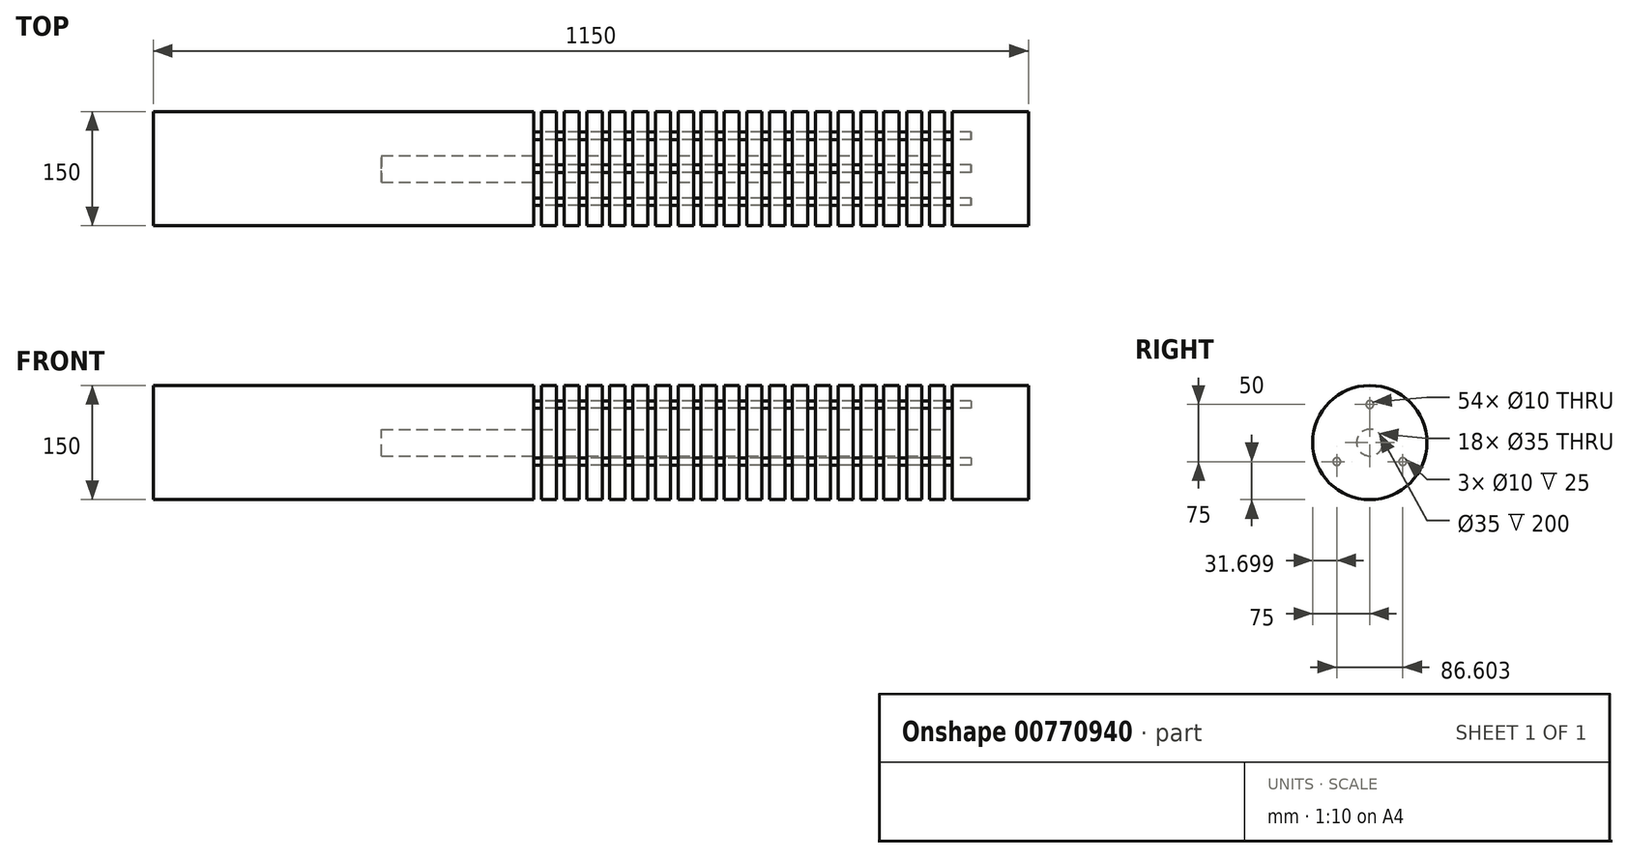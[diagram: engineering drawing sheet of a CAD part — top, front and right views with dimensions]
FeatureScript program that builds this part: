
annotation { "Feature Type Name" : "Feature", "Feature Type Description" : "" }
export const myFeature = defineFeature(function(context is Context, id is Id, definition is map)
    precondition{}
    {
        {
            var Q0;
            Q0=qCreatedBy(makeId("Top.planeOp"),FACE);
            var sketch = newSketch(context, id + "F0", { "sketchPlane" : qUnion([Q0])});
            skLineSegment(sketch, "E0", {"start": v(-500, 0) * mm, "end": v(-500, -75) * mm});
            skLineSegment(sketch, "E1", {"start": v(-500, -75) * mm, "end": v(0, -75) * mm});
            skLineSegment(sketch, "E2", {"start": v(0, -75) * mm, "end": v(0, -17.5) * mm});
            skLineSegment(sketch, "E3", {"start": v(0, -17.5) * mm, "end": v(-200, -17.5) * mm});
            skLineSegment(sketch, "E4", {"start": v(-200, -17.5) * mm, "end": v(-200, 0) * mm});
            skLineSegment(sketch, "E5", {"start": v(-200, 0) * mm, "end": v(-500, 0) * mm});
            skSolve(sketch);
        }
        {
            var Q0;
            Q0=qCreatedBy(makeId("Top.planeOp"),FACE);
            var sketch = newSketch(context, id + "F1", { "sketchPlane" : qUnion([Q0])});
            skLineSegment(sketch, "E6.bottom", {"start": v(10, -17.5) * mm, "end": v(30, -17.5) * mm});
            skLineSegment(sketch, "E6.top", {"start": v(10, -75) * mm, "end": v(30, -75) * mm});
            skLineSegment(sketch, "E6.left", {"start": v(10, -17.5) * mm, "end": v(10, -75) * mm});
            skLineSegment(sketch, "E6.right", {"start": v(30, -17.5) * mm, "end": v(30, -75) * mm});
            skLineSegment(sketch, "E7.1.0.0", {"start": v(40, -75) * mm, "end": v(60, -75) * mm});
            skLineSegment(sketch, "E7.1.0.1", {"start": v(60, -17.5) * mm, "end": v(60, -75) * mm});
            skLineSegment(sketch, "E7.1.0.2", {"start": v(40, -17.5) * mm, "end": v(40, -75) * mm});
            skLineSegment(sketch, "E7.1.0.3", {"start": v(40, -17.5) * mm, "end": v(60, -17.5) * mm});
            skLineSegment(sketch, "E7.2.0.0", {"start": v(70, -75) * mm, "end": v(90, -75) * mm});
            skLineSegment(sketch, "E7.2.0.1", {"start": v(90, -17.5) * mm, "end": v(90, -75) * mm});
            skLineSegment(sketch, "E7.2.0.2", {"start": v(70, -17.5) * mm, "end": v(70, -75) * mm});
            skLineSegment(sketch, "E7.2.0.3", {"start": v(70, -17.5) * mm, "end": v(90, -17.5) * mm});
            skLineSegment(sketch, "E7.3.0.0", {"start": v(100, -75) * mm, "end": v(120, -75) * mm});
            skLineSegment(sketch, "E7.3.0.1", {"start": v(120, -17.5) * mm, "end": v(120, -75) * mm});
            skLineSegment(sketch, "E7.3.0.2", {"start": v(100, -17.5) * mm, "end": v(100, -75) * mm});
            skLineSegment(sketch, "E7.3.0.3", {"start": v(100, -17.5) * mm, "end": v(120, -17.5) * mm});
            skLineSegment(sketch, "E7.4.0.0", {"start": v(130, -75) * mm, "end": v(150, -75) * mm});
            skLineSegment(sketch, "E7.4.0.1", {"start": v(150, -17.5) * mm, "end": v(150, -75) * mm});
            skLineSegment(sketch, "E7.4.0.2", {"start": v(130, -17.5) * mm, "end": v(130, -75) * mm});
            skLineSegment(sketch, "E7.4.0.3", {"start": v(130, -17.5) * mm, "end": v(150, -17.5) * mm});
            skLineSegment(sketch, "E7.5.0.0", {"start": v(160, -75) * mm, "end": v(180, -75) * mm});
            skLineSegment(sketch, "E7.5.0.1", {"start": v(180, -17.5) * mm, "end": v(180, -75) * mm});
            skLineSegment(sketch, "E7.5.0.2", {"start": v(160, -17.5) * mm, "end": v(160, -75) * mm});
            skLineSegment(sketch, "E7.5.0.3", {"start": v(160, -17.5) * mm, "end": v(180, -17.5) * mm});
            skLineSegment(sketch, "E7.6.0.0", {"start": v(190, -75) * mm, "end": v(210, -75) * mm});
            skLineSegment(sketch, "E7.6.0.1", {"start": v(210, -17.5) * mm, "end": v(210, -75) * mm});
            skLineSegment(sketch, "E7.6.0.2", {"start": v(190, -17.5) * mm, "end": v(190, -75) * mm});
            skLineSegment(sketch, "E7.6.0.3", {"start": v(190, -17.5) * mm, "end": v(210, -17.5) * mm});
            skLineSegment(sketch, "E7.7.0.0", {"start": v(220, -75) * mm, "end": v(240, -75) * mm});
            skLineSegment(sketch, "E7.7.0.1", {"start": v(240, -17.5) * mm, "end": v(240, -75) * mm});
            skLineSegment(sketch, "E7.7.0.2", {"start": v(220, -17.5) * mm, "end": v(220, -75) * mm});
            skLineSegment(sketch, "E7.7.0.3", {"start": v(220, -17.5) * mm, "end": v(240, -17.5) * mm});
            skLineSegment(sketch, "E7.8.0.0", {"start": v(250, -75) * mm, "end": v(270, -75) * mm});
            skLineSegment(sketch, "E7.8.0.1", {"start": v(270, -17.5) * mm, "end": v(270, -75) * mm});
            skLineSegment(sketch, "E7.8.0.2", {"start": v(250, -17.5) * mm, "end": v(250, -75) * mm});
            skLineSegment(sketch, "E7.8.0.3", {"start": v(250, -17.5) * mm, "end": v(270, -17.5) * mm});
            skLineSegment(sketch, "E7.9.0.0", {"start": v(280, -75) * mm, "end": v(300, -75) * mm});
            skLineSegment(sketch, "E7.9.0.1", {"start": v(300, -17.5) * mm, "end": v(300, -75) * mm});
            skLineSegment(sketch, "E7.9.0.2", {"start": v(280, -17.5) * mm, "end": v(280, -75) * mm});
            skLineSegment(sketch, "E7.9.0.3", {"start": v(280, -17.5) * mm, "end": v(300, -17.5) * mm});
            skLineSegment(sketch, "E7.10.0.0", {"start": v(310, -75) * mm, "end": v(330, -75) * mm});
            skLineSegment(sketch, "E7.10.0.1", {"start": v(330, -17.5) * mm, "end": v(330, -75) * mm});
            skLineSegment(sketch, "E7.10.0.2", {"start": v(310, -17.5) * mm, "end": v(310, -75) * mm});
            skLineSegment(sketch, "E7.10.0.3", {"start": v(310, -17.5) * mm, "end": v(330, -17.5) * mm});
            skLineSegment(sketch, "E7.11.0.0", {"start": v(340, -75) * mm, "end": v(360, -75) * mm});
            skLineSegment(sketch, "E7.11.0.1", {"start": v(360, -17.5) * mm, "end": v(360, -75) * mm});
            skLineSegment(sketch, "E7.11.0.2", {"start": v(340, -17.5) * mm, "end": v(340, -75) * mm});
            skLineSegment(sketch, "E7.11.0.3", {"start": v(340, -17.5) * mm, "end": v(360, -17.5) * mm});
            skLineSegment(sketch, "E7.12.0.0", {"start": v(370, -75) * mm, "end": v(390, -75) * mm});
            skLineSegment(sketch, "E7.12.0.1", {"start": v(390, -17.5) * mm, "end": v(390, -75) * mm});
            skLineSegment(sketch, "E7.12.0.2", {"start": v(370, -17.5) * mm, "end": v(370, -75) * mm});
            skLineSegment(sketch, "E7.12.0.3", {"start": v(370, -17.5) * mm, "end": v(390, -17.5) * mm});
            skLineSegment(sketch, "E7.13.0.0", {"start": v(400, -75) * mm, "end": v(420, -75) * mm});
            skLineSegment(sketch, "E7.13.0.1", {"start": v(420, -17.5) * mm, "end": v(420, -75) * mm});
            skLineSegment(sketch, "E7.13.0.2", {"start": v(400, -17.5) * mm, "end": v(400, -75) * mm});
            skLineSegment(sketch, "E7.13.0.3", {"start": v(400, -17.5) * mm, "end": v(420, -17.5) * mm});
            skLineSegment(sketch, "E7.14.0.0", {"start": v(430, -75) * mm, "end": v(450, -75) * mm});
            skLineSegment(sketch, "E7.14.0.1", {"start": v(450, -17.5) * mm, "end": v(450, -75) * mm});
            skLineSegment(sketch, "E7.14.0.2", {"start": v(430, -17.5) * mm, "end": v(430, -75) * mm});
            skLineSegment(sketch, "E7.14.0.3", {"start": v(430, -17.5) * mm, "end": v(450, -17.5) * mm});
            skLineSegment(sketch, "E7.15.0.0", {"start": v(460, -75) * mm, "end": v(480, -75) * mm});
            skLineSegment(sketch, "E7.15.0.1", {"start": v(480, -17.5) * mm, "end": v(480, -75) * mm});
            skLineSegment(sketch, "E7.15.0.2", {"start": v(460, -17.5) * mm, "end": v(460, -75) * mm});
            skLineSegment(sketch, "E7.15.0.3", {"start": v(460, -17.5) * mm, "end": v(480, -17.5) * mm});
            skLineSegment(sketch, "E7.16.0.0", {"start": v(490, -75) * mm, "end": v(510, -75) * mm});
            skLineSegment(sketch, "E7.16.0.1", {"start": v(510, -17.5) * mm, "end": v(510, -75) * mm});
            skLineSegment(sketch, "E7.16.0.2", {"start": v(490, -17.5) * mm, "end": v(490, -75) * mm});
            skLineSegment(sketch, "E7.16.0.3", {"start": v(490, -17.5) * mm, "end": v(510, -17.5) * mm});
            skLineSegment(sketch, "E7.17.0.0", {"start": v(520, -75) * mm, "end": v(540, -75) * mm});
            skLineSegment(sketch, "E7.17.0.1", {"start": v(540, -17.5) * mm, "end": v(540, -75) * mm});
            skLineSegment(sketch, "E7.17.0.2", {"start": v(520, -17.5) * mm, "end": v(520, -75) * mm});
            skLineSegment(sketch, "E7.17.0.3", {"start": v(520, -17.5) * mm, "end": v(540, -17.5) * mm});
            skLineSegment(sketch, "E7.direction1", {"start": v(10, -75) * mm, "end": v(40, -75) * mm, "construction": true});
            skSolve(sketch);
        }
        {
            var Q0;
            Q0=qCreatedBy(makeId("Top.planeOp"),FACE);
            var sketch = newSketch(context, id + "F2", { "sketchPlane" : qUnion([Q0])});
            skLineSegment(sketch, "E8.bottom", {"start": v(550, -75) * mm, "end": v(650, -75) * mm});
            skLineSegment(sketch, "E8.top", {"start": v(550, 0) * mm, "end": v(650, 0) * mm});
            skLineSegment(sketch, "E8.left", {"start": v(550, -75) * mm, "end": v(550, 0) * mm});
            skLineSegment(sketch, "E8.right", {"start": v(650, -75) * mm, "end": v(650, 0) * mm});
            skSolve(sketch);
        }
        {
            var Q0;
            Q0=makeQuery(id+"F0.imprint","IMPRINT",FACE,{"disambiguationData":[TD([[makeQuery(id+"F0.imprint","IMPRINT",EDGE,{"derivedFrom":sQuery(id+"F0.wireOp",EDGE,"E0")}),1.0]])]});
            var Q1;
            Q1=makeQuery(id+"F1.imprint","IMPRINT",FACE,{"disambiguationData":[TD([[makeQuery(id+"F1.imprint","IMPRINT",EDGE,{"derivedFrom":sQuery(id+"F1.wireOp",EDGE,"E7.4.0.0")}),1.0]])]});
            var Q2;
            Q2=makeQuery(id+"F1.imprint","IMPRINT",FACE,{"disambiguationData":[TD([[makeQuery(id+"F1.imprint","IMPRINT",EDGE,{"derivedFrom":sQuery(id+"F1.wireOp",EDGE,"E7.9.0.0")}),1.0]])]});
            var Q3;
            Q3=makeQuery(id+"F1.imprint","IMPRINT",FACE,{"disambiguationData":[TD([[makeQuery(id+"F1.imprint","IMPRINT",EDGE,{"derivedFrom":sQuery(id+"F1.wireOp",EDGE,"E7.3.0.0")}),1.0]])]});
            var Q4;
            Q4=makeQuery(id+"F1.imprint","IMPRINT",FACE,{"disambiguationData":[TD([[makeQuery(id+"F1.imprint","IMPRINT",EDGE,{"derivedFrom":sQuery(id+"F1.wireOp",EDGE,"E7.2.0.0")}),1.0]])]});
            var Q5;
            Q5=makeQuery(id+"F1.imprint","IMPRINT",FACE,{"disambiguationData":[TD([[makeQuery(id+"F1.imprint","IMPRINT",EDGE,{"derivedFrom":sQuery(id+"F1.wireOp",EDGE,"E7.10.0.0")}),1.0]])]});
            var Q6;
            Q6=makeQuery(id+"F1.imprint","IMPRINT",FACE,{"disambiguationData":[TD([[makeQuery(id+"F1.imprint","IMPRINT",EDGE,{"derivedFrom":sQuery(id+"F1.wireOp",EDGE,"E7.1.0.0")}),1.0]])]});
            var Q7;
            Q7=makeQuery(id+"F1.imprint","IMPRINT",FACE,{"disambiguationData":[TD([[makeQuery(id+"F1.imprint","IMPRINT",EDGE,{"derivedFrom":sQuery(id+"F1.wireOp",EDGE,"E7.8.0.0")}),1.0]])]});
            var Q8;
            Q8=makeQuery(id+"F1.imprint","IMPRINT",FACE,{"disambiguationData":[TD([[makeQuery(id+"F1.imprint","IMPRINT",EDGE,{"derivedFrom":sQuery(id+"F1.wireOp",EDGE,"E7.17.0.0")}),1.0]])]});
            var Q9;
            Q9=makeQuery(id+"F1.imprint","IMPRINT",FACE,{"disambiguationData":[TD([[makeQuery(id+"F1.imprint","IMPRINT",EDGE,{"derivedFrom":sQuery(id+"F1.wireOp",EDGE,"E7.16.0.0")}),1.0]])]});
            var Q10;
            Q10=makeQuery(id+"F1.imprint","IMPRINT",FACE,{"disambiguationData":[TD([[makeQuery(id+"F1.imprint","IMPRINT",EDGE,{"derivedFrom":sQuery(id+"F1.wireOp",EDGE,"E7.12.0.0")}),1.0]])]});
            var Q11;
            Q11=makeQuery(id+"F1.imprint","IMPRINT",FACE,{"disambiguationData":[TD([[makeQuery(id+"F1.imprint","IMPRINT",EDGE,{"derivedFrom":sQuery(id+"F1.wireOp",EDGE,"E7.5.0.0")}),1.0]])]});
            var Q12;
            Q12=makeQuery(id+"F1.imprint","IMPRINT",FACE,{"disambiguationData":[TD([[makeQuery(id+"F1.imprint","IMPRINT",EDGE,{"derivedFrom":sQuery(id+"F1.wireOp",EDGE,"E7.6.0.0")}),1.0]])]});
            var Q13;
            Q13=makeQuery(id+"F1.imprint","IMPRINT",FACE,{"disambiguationData":[TD([[makeQuery(id+"F1.imprint","IMPRINT",EDGE,{"derivedFrom":sQuery(id+"F1.wireOp",EDGE,"E7.11.0.0")}),1.0]])]});
            var Q14;
            Q14=makeQuery(id+"F1.imprint","IMPRINT",FACE,{"disambiguationData":[TD([[makeQuery(id+"F1.imprint","IMPRINT",EDGE,{"derivedFrom":sQuery(id+"F1.wireOp",EDGE,"E7.7.0.0")}),1.0]])]});
            var Q15;
            Q15=makeQuery(id+"F1.imprint","IMPRINT",FACE,{"disambiguationData":[TD([[makeQuery(id+"F1.imprint","IMPRINT",EDGE,{"derivedFrom":sQuery(id+"F1.wireOp",EDGE,"E6.bottom")}),-1.0]])]});
            var Q16;
            Q16=makeQuery(id+"F1.imprint","IMPRINT",FACE,{"disambiguationData":[TD([[makeQuery(id+"F1.imprint","IMPRINT",EDGE,{"derivedFrom":sQuery(id+"F1.wireOp",EDGE,"E7.14.0.0")}),1.0]])]});
            var Q17;
            Q17=makeQuery(id+"F1.imprint","IMPRINT",FACE,{"disambiguationData":[TD([[makeQuery(id+"F1.imprint","IMPRINT",EDGE,{"derivedFrom":sQuery(id+"F1.wireOp",EDGE,"E7.13.0.0")}),1.0]])]});
            var Q18;
            Q18=makeQuery(id+"F2.imprint","IMPRINT",FACE,{"disambiguationData":[TD([[makeQuery(id+"F2.imprint","IMPRINT",EDGE,{"derivedFrom":sQuery(id+"F2.wireOp",EDGE,"E8.bottom")}),1.0]])]});
            var Q19;
            Q19=makeQuery(id+"F1.imprint","IMPRINT",FACE,{"disambiguationData":[TD([[makeQuery(id+"F1.imprint","IMPRINT",EDGE,{"derivedFrom":sQuery(id+"F1.wireOp",EDGE,"E7.15.0.0")}),1.0]])]});
            var Q20;
            Q20=sQuery(id+"F0.wireOp",EDGE,"E5");
            revolve(context, id + "F3", {"surfaceOperationType" : NewSurfaceOperationType.NEW, "entities" : qUnion([Q0, Q1, Q2, Q3, Q4, Q5, Q6, Q7, Q8, Q9, Q10, Q11, Q12, Q13, Q14, Q15, Q16, Q17, Q18, Q19]), "axis" : qUnion([Q20]), "revolveType" : RevolveType.FULL});
        }
        {
            var Q0;
            Q0=qCreatedBy(makeId("Right.planeOp"),FACE);
            var sketch = newSketch(context, id + "F4", { "sketchPlane" : qUnion([Q0])});
            skCircle(sketch, "E9", {"center": v(0, 50) * mm, "radius": 5 * mm});
            skCircle(sketch, "E10.1.0", {"center": v(-43.3, -25) * mm, "radius": 5 * mm});
            skCircle(sketch, "E10.2.0", {"center": v(43.3, -25) * mm, "radius": 5 * mm});
            skPoint(sketch, "E10.center", {"position": v(0, 0) * mm});
            skSolve(sketch);
        }
        {
            var Q0;
            Q0=qSketchRegion(id+"F4",true);
            var Q1;
            Q1=makeQuery(id+"F3.opRevolve","SWEPT_FACE",FACE,{"disambiguationData":[OSD([sQuery(id+"F2.wireOp",EDGE,"E8.left")])]});
            extrude(context, id + "F5", {"entities" : qUnion([Q0]), "operationType" : NewBodyOperationType.REMOVE, "endBound" : BoundingType.UP_TO_SURFACE, "depth" : 25 * mm, "endBoundEntityFace" : qUnion([Q1]), "hasOffset" : true, "offsetDistance" : 25 * mm, "offsetOppositeDirection" : true});
        }
        {
            var Q0;
            Q0=qSketchRegion(id+"F4",true);
            var Q1;
            Q1=makeQuery(id+"F3.opRevolve","SWEPT_FACE",FACE,{"disambiguationData":[OSD([sQuery(id+"F2.wireOp",EDGE,"E8.left")])]});
            extrude(context, id + "F6", {"entities" : qUnion([Q0]), "endBound" : BoundingType.UP_TO_SURFACE, "depth" : 25 * mm, "endBoundEntityFace" : qUnion([Q1]), "hasOffset" : true, "offsetDistance" : 25 * mm, "offsetOppositeDirection" : true});
        }
    });
